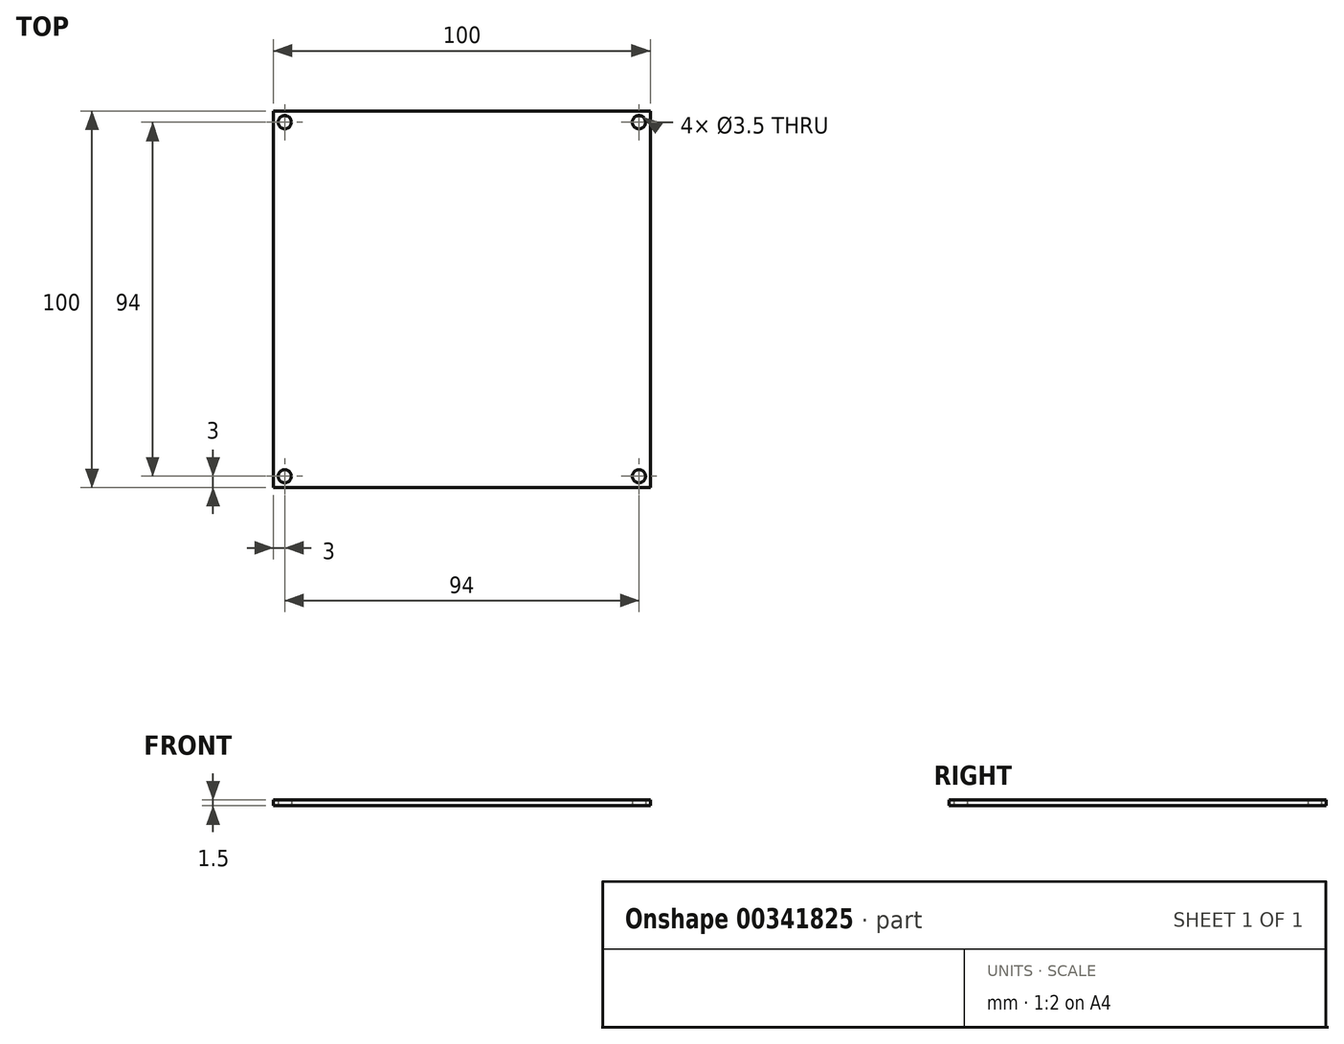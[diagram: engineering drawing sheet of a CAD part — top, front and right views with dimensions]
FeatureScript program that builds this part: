
annotation { "Feature Type Name" : "Feature", "Feature Type Description" : "" }
export const myFeature = defineFeature(function(context is Context, id is Id, definition is map)
    precondition{}
    {
        {
            var Q0;
            Q0=qCreatedBy(makeId("Top.planeOp"),FACE);
            var sketch = newSketch(context, id + "F0", { "sketchPlane" : qUnion([Q0])});
            skLineSegment(sketch, "E0.bottom", {"start": v(0, 0) * mm, "end": v(100, 0) * mm});
            skLineSegment(sketch, "E0.top", {"start": v(0, 100) * mm, "end": v(100, 100) * mm});
            skLineSegment(sketch, "E0.left", {"start": v(0, 0) * mm, "end": v(0, 100) * mm});
            skLineSegment(sketch, "E0.right", {"start": v(100, 0) * mm, "end": v(100, 100) * mm});
            skCircle(sketch, "E1", {"center": v(3, 97) * mm, "radius": 1.75 * mm});
            skCircle(sketch, "E2", {"center": v(97, 97) * mm, "radius": 1.75 * mm});
            skCircle(sketch, "E3", {"center": v(97, 3) * mm, "radius": 1.75 * mm});
            skCircle(sketch, "E4", {"center": v(3, 3) * mm, "radius": 1.75 * mm});
            skSolve(sketch);
        }
        {
            var Q0;
            Q0=makeQuery(id+"F0.imprint","IMPRINT",FACE,{"disambiguationData":[TD([[makeQuery(id+"F0.imprint","IMPRINT",EDGE,{"derivedFrom":sQuery(id+"F0.wireOp",EDGE,"E0.bottom")}),1.0]])]});
            extrude(context, id + "F1", {"entities" : qUnion([Q0]), "depth" : 1.5 * mm});
        }
    });
